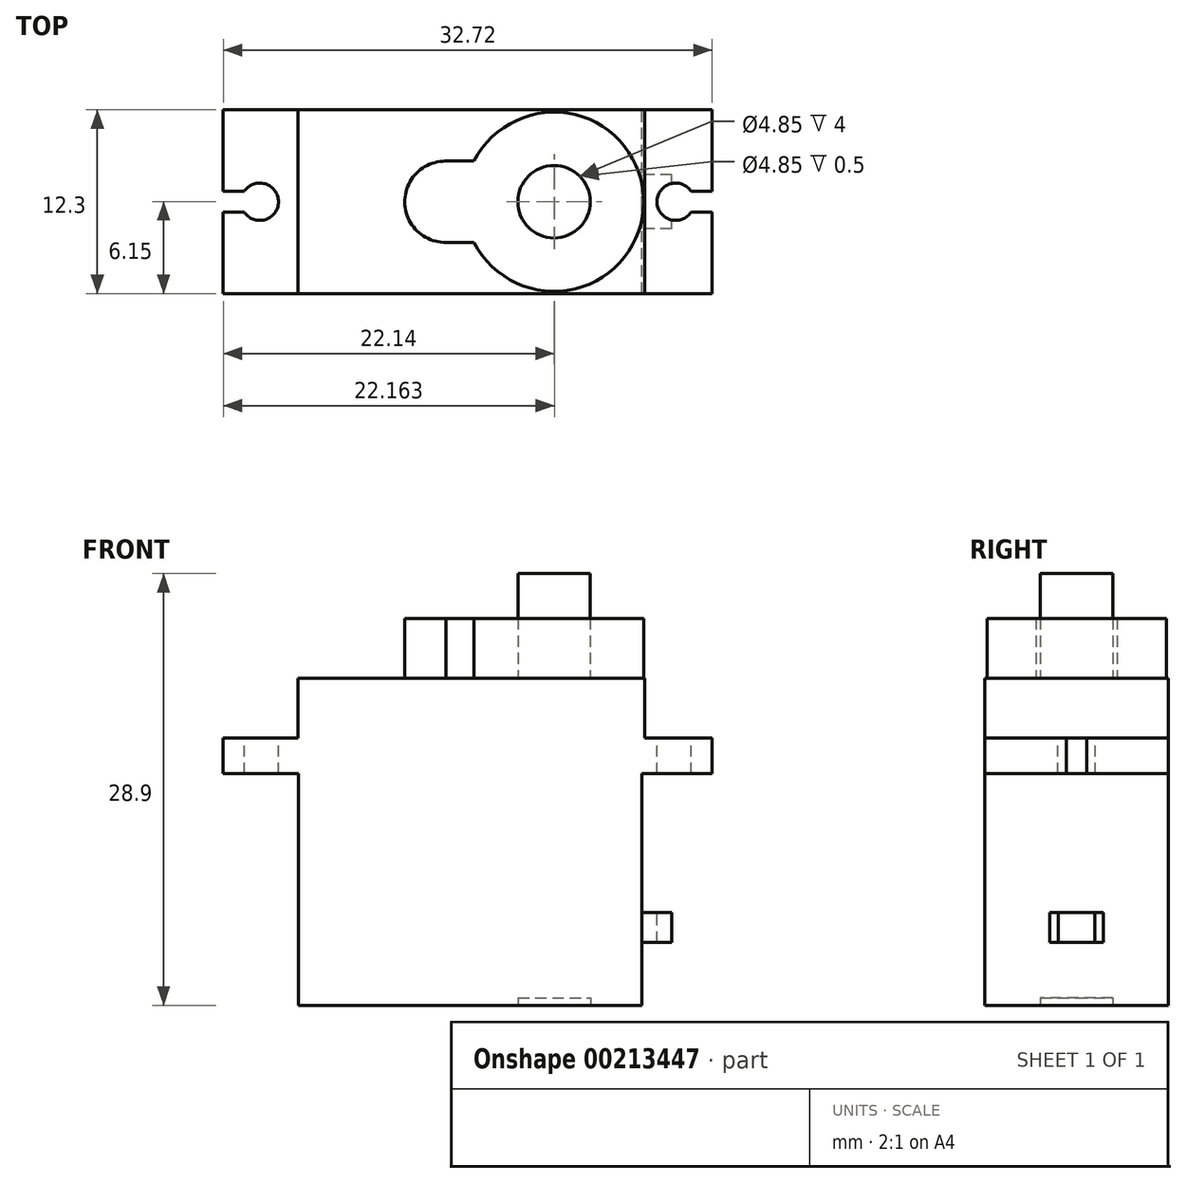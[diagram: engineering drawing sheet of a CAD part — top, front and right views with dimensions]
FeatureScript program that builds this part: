
annotation { "Feature Type Name" : "Feature", "Feature Type Description" : "" }
export const myFeature = defineFeature(function(context is Context, id is Id, definition is map)
    precondition{}
    {
        {
            var Q0;
            Q0=qCreatedBy(makeId("Front.planeOp"),FACE);
            var sketch = newSketch(context, id + "F0", { "sketchPlane" : qUnion([Q0])});
            skLineSegment(sketch, "E0.bottom", {"start": v(-11.5, 0) * mm, "end": v(11.5, 0) * mm});
            skLineSegment(sketch, "E0.top", {"start": v(-11.5, -15.5) * mm, "end": v(11.5, -15.5) * mm});
            skLineSegment(sketch, "E0.left", {"start": v(-11.5, 0) * mm, "end": v(-11.5, -15.5) * mm});
            skLineSegment(sketch, "E0.right", {"start": v(11.5, 0) * mm, "end": v(11.5, -15.5) * mm});
            skLineSegment(sketch, "E1", {"start": v(11.5, 0) * mm, "end": v(16.2, 0) * mm});
            skLineSegment(sketch, "E2", {"start": v(16.2, 0) * mm, "end": v(16.2, 2.4) * mm});
            skLineSegment(sketch, "E3", {"start": v(16.2, 2.4) * mm, "end": v(11.7, 2.4) * mm});
            skLineSegment(sketch, "E4", {"start": v(11.7, 2.4) * mm, "end": v(11.7, 6.4) * mm});
            skLineSegment(sketch, "E5", {"start": v(11.7, 6.4) * mm, "end": v(-11.52, 6.4) * mm});
            skLineSegment(sketch, "E6", {"start": v(-11.52, 6.4) * mm, "end": v(-11.52, 2.4) * mm});
            skLineSegment(sketch, "E7", {"start": v(-11.52, 2.4) * mm, "end": v(-16.52, 2.4) * mm});
            skLineSegment(sketch, "E8", {"start": v(-16.52, 2.4) * mm, "end": v(-16.52, 0) * mm});
            skLineSegment(sketch, "E9", {"start": v(-16.52, 0) * mm, "end": v(-11.5, 0) * mm});
            skSolve(sketch);
        }
        {
            var Q0;
            Q0 = qSketchRegion(id + "F0", true);
            extrude(context, id + "F1", {"entities" : qUnion([Q0]), "depth" : 12.3 * mm});
        }
        {
            var Q0;
            Q0=makeQuery(id+"F1.opExtrude","SWEPT_FACE",FACE,{"disambiguationData":[OSD([sQuery(id+"F0.wireOp",EDGE,"E5")])]});
            var sketch = newSketch(context, id + "F2", { "sketchPlane" : qUnion([Q0])});
            skLineSegment(sketch, "E10", {"start": v(11.7, -6.15) * mm, "end": v(11.62, -6.15) * mm});
            skArc(sketch, "E11", {"start": v(0.27, -8.87) * mm, "mid": v(11.62, -6.15) * mm, "end": v(0.27, -3.43) * mm});
            skPoint(sketch, "E12", {"position": v(-11.52, -6.15) * mm});
            skArc(sketch, "E13", {"start": v(-1.64, -3.43) * mm, "mid": v(-4.37, -6.17) * mm, "end": v(-1.6, -8.87) * mm});
            skLineSegment(sketch, "E14", {"start": v(-1.67, -3.43) * mm, "end": v(0.27, -3.43) * mm});
            skLineSegment(sketch, "E15", {"start": v(-1.6, -8.87) * mm, "end": v(0.27, -8.87) * mm});
            skCircle(sketch, "E16", {"center": v(5.62, -6.15) * mm, "radius": 2.43 * mm});
            skSolve(sketch);
        }
        {
            var Q0;
            {var subQ4=sQuery(id+"F2.wireOp",EDGE,"E15");Q0=makeQuery(id+"F2.imprint","IMPRINT",FACE,{"disambiguationData":[TD([[makeQuery(id+"F2.imprint","IMPRINT",EDGE,{"derivedFrom":subQ4}),1.0]])]});}
            extrude(context, id + "F3", {"entities" : qUnion([Q0]), "operationType" : NewBodyOperationType.ADD, "depth" : 4 * mm});
        }
        {
            var Q0;
            Q0=makeQuery(id+"F3.boolean.opBoolean","SPLIT",FACE,{"disambiguationData":[TD([makeQuery(id+"F3.opExtrude","SWEPT_FACE",FACE,{"disambiguationData":[OSD([sQuery(id+"F2.wireOp",EDGE,"E16")])]})])],"derivedFrom":makeQuery(id+"F1.opExtrude","SWEPT_FACE",FACE,{"disambiguationData":[OSD([sQuery(id+"F0.wireOp",EDGE,"E5")])]})});
            extrude(context, id + "F4", {"entities" : qUnion([Q0]), "depth" : 7 * mm});
        }
        {
            var Q0;
            Q0=makeQuery(id+"F1.opExtrude","SWEPT_FACE",FACE,{"disambiguationData":[OSD([sQuery(id+"F0.wireOp",EDGE,"E0.right")])]});
            var sketch = newSketch(context, id + "F5", { "sketchPlane" : qUnion([Q0])});
            skLineSegment(sketch, "E17.bottom", {"start": v(-7.95, -9.3) * mm, "end": v(-4.35, -9.3) * mm});
            skLineSegment(sketch, "E17.top", {"start": v(-7.95, -11.3) * mm, "end": v(-4.35, -11.3) * mm});
            skLineSegment(sketch, "E17.left", {"start": v(-7.95, -9.3) * mm, "end": v(-7.95, -11.3) * mm});
            skLineSegment(sketch, "E17.right", {"start": v(-4.35, -9.3) * mm, "end": v(-4.35, -11.3) * mm});
            skPoint(sketch, "E18", {"position": v(-6.15, -11.3) * mm});
            skSolve(sketch);
        }
        {
            var Q0;
            Q0=makeQuery(id+"F5.imprint","IMPRINT",FACE,{"disambiguationData":[TD([[makeQuery(id+"F5.imprint","IMPRINT",EDGE,{"derivedFrom":sQuery(id+"F5.wireOp",EDGE,"E17.bottom")}),-1.0]])]});
            extrude(context, id + "F6", {"entities" : qUnion([Q0]), "depth" : 2 * mm});
        }
        {
            var Q0;
            Q0=makeQuery(id+"F1.opExtrude","SWEPT_FACE",FACE,{"disambiguationData":[OSD([sQuery(id+"F0.wireOp",EDGE,"E3")])]});
            var sketch = newSketch(context, id + "F7", { "sketchPlane" : qUnion([Q0])});
            skLineSegment(sketch, "E19", {"start": v(16.2, -5.46) * mm, "end": v(14.8, -5.46) * mm});
            skLineSegment(sketch, "E20", {"start": v(14.8, -6.84) * mm, "end": v(16.2, -6.84) * mm});
            skLineSegment(sketch, "E21", {"start": v(16.2, -5.46) * mm, "end": v(16.2, -6.84) * mm});
            skArc(sketch, "E22", {"start": v(14.8, -5.46) * mm, "mid": v(12.5, -6.15) * mm, "end": v(14.8, -6.84) * mm});
            skPoint(sketch, "E22.centerSnap0", {"position": v(14.8, -6.15) * mm});
            skSolve(sketch);
        }
        {
            var Q0;
            Q0=makeQuery(id+"F7.imprint","IMPRINT",FACE,{"disambiguationData":[TD([[makeQuery(id+"F7.imprint","IMPRINT",EDGE,{"derivedFrom":sQuery(id+"F7.wireOp",EDGE,"E19")}),1.0]])]});
            extrude(context, id + "F8", {"entities" : qUnion([Q0]), "operationType" : NewBodyOperationType.REMOVE, "endBound" : BoundingType.THROUGH_ALL, "oppositeDirection" : true, "depth" : 25 * mm});
        }
        {
            var Q0;
            Q0=makeQuery(id+"F1.opExtrude","SWEPT_FACE",FACE,{"disambiguationData":[OSD([sQuery(id+"F0.wireOp",EDGE,"E7")])]});
            var sketch = newSketch(context, id + "F9", { "sketchPlane" : qUnion([Q0])});
            skPoint(sketch, "E23", {"position": v(-16.52, -6.84) * mm});
            skPoint(sketch, "E24", {"position": v(-16.52, -5.46) * mm});
            skPoint(sketch, "E25", {"position": v(-15.12, -5.46) * mm});
            skPoint(sketch, "E26", {"position": v(-15.12, -6.84) * mm});
            skArc(sketch, "E27", {"start": v(-15.12, -6.84) * mm, "mid": v(-12.83, -6.15) * mm, "end": v(-15.12, -5.46) * mm});
            skPoint(sketch, "E27.centerSnap0", {"position": v(-16.52, -6.15) * mm});
            skLineSegment(sketch, "E28", {"start": v(-15.12, -6.84) * mm, "end": v(-16.52, -6.84) * mm});
            skLineSegment(sketch, "E29", {"start": v(-16.52, -5.46) * mm, "end": v(-15.12, -5.46) * mm});
            skLineSegment(sketch, "E30", {"start": v(-16.52, -5.46) * mm, "end": v(-16.52, -6.84) * mm});
            skSolve(sketch);
        }
        {
            var Q0;
            Q0=makeQuery(id+"F9.imprint","IMPRINT",FACE,{"disambiguationData":[TD([[makeQuery(id+"F9.imprint","IMPRINT",EDGE,{"derivedFrom":sQuery(id+"F9.wireOp",EDGE,"E27")}),1.0]])]});
            extrude(context, id + "F10", {"entities" : qUnion([Q0]), "operationType" : NewBodyOperationType.REMOVE, "endBound" : BoundingType.THROUGH_ALL, "oppositeDirection" : true, "depth" : 25 * mm});
        }
        {
            var Q0;
            Q0=makeQuery(id+"F1.opExtrude","SWEPT_FACE",FACE,{"disambiguationData":[OSD([sQuery(id+"F0.wireOp",EDGE,"E0.top")])]});
            var sketch = newSketch(context, id + "F11", { "sketchPlane" : qUnion([Q0])});
            skCircle(sketch, "E31", {"center": v(5.64, 6.15) * mm, "radius": 2.43 * mm});
            skPoint(sketch, "E31.centerSnap0", {"position": v(-11.5, 6.15) * mm});
            skSolve(sketch);
        }
        {
            var Q0;
            Q0=makeQuery(id+"F11.imprint","IMPRINT",FACE,{"disambiguationData":[TD([[makeQuery(id+"F11.imprint","IMPRINT",EDGE,{"derivedFrom":sQuery(id+"F11.wireOp",EDGE,"E31")}),1.0]])]});
            extrude(context, id + "F12", {"entities" : qUnion([Q0]), "operationType" : NewBodyOperationType.REMOVE, "oppositeDirection" : true, "depth" : .5 * mm});
        }
    });
